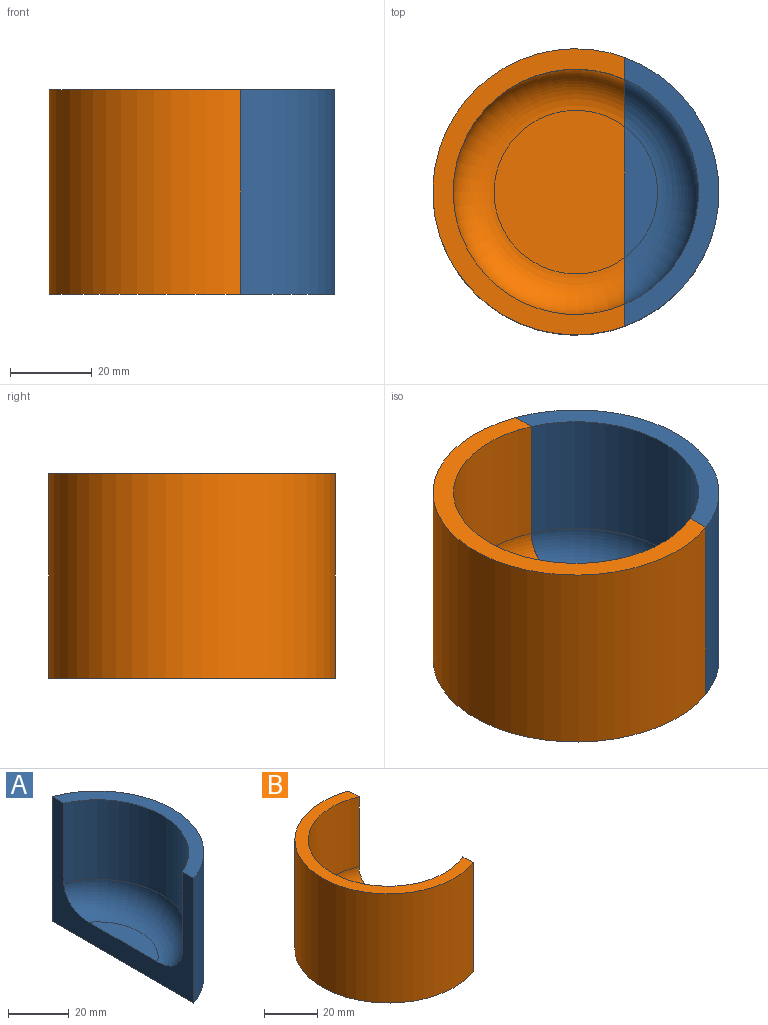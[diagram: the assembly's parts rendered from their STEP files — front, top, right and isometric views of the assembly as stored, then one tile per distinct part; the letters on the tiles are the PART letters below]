
ASSEMBLY  parts=2 mates=1
PART A: 7 faces, bbox 29.8x65.8x50 mm
  f0: plane 32x8mm, normal (0,0,1), area 178.9mm2, adj f5,f6
  f1: plane 65.76x23mm, normal (0,0,-1), area 1101mm2, adj f2,f6
  f2: cylinder r=35mm len=65.76mm, axis (0,0,-1), area 4272.9mm2, adj f1,f3,f6
  f3: plane 65.76x23mm, normal (0,0,1), area 387.6mm2, adj f2,f4,f6
  f4: cylinder r=30mm len=54.99mm, axis (0,0,-1), area 2225.8mm2, adj f3,f5,f6
  f5: torus R=20mm, axis (0,0,1), area 908.8mm2, adj f0,f4,f6
  f6: plane 65.76x50mm, normal (-1,0,0), area 1025.9mm2, adj f0,f1,f2,f3,f4,f5
PART B: 7 faces, bbox 54.5x70x50 mm
  f0: plane 65.76x50mm, normal (1,0,0), area 1025.9mm2, adj f1,f2,f3,f4,f5,f6
  f1: torus R=20mm, axis (0,0,1), area 1693.4mm2, adj f0,f2,f6
  f2: cylinder r=30mm len=60mm, axis (0,0,-1), area 3806mm2, adj f0,f1,f3
  f3: plane 70x47mm, normal (0,0,1), area 633.4mm2, adj f0,f2,f4
  f4: cylinder r=35mm len=70mm, axis (0,0,-1), area 6722.6mm2, adj f0,f3,f5
  f5: plane 70x47mm, normal (0,0,-1), area 2747.5mm2, adj f0,f4
  f6: plane 40x32mm, normal (0,0,1), area 1077.7mm2, adj f0,f1
PLACE A t=(-45.5,49.96,-29.52)mm
PLACE B t=(-45.5,49.96,-29.52)mm
MATE fastened A.f6 <-> B.f0  axis (-1,0,0) through (116.5,49.96,-21.52)mm
